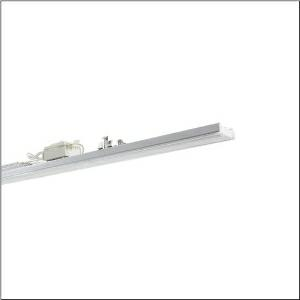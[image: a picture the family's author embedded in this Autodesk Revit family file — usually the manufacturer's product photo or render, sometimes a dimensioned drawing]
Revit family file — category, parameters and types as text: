
# Revit family: licross_r__21_recessed_mo_52te11dv4dxg_417d
name_source: partatom
category: Lighting Fixtures
units: mm (PartAtom-declared; Revit-internal decimal feet)

## family parameters
Cut with Voids When Loaded = No
Host = Face
Light Source = No
Part Type = Normal
Room Calculation Point = No
Round Connector Dimension = Use Diameter
Shared = No

## types (1)
- --- (1 x LED, 13000 lm, 72.2 W, 4000K)
    Apparent Load = 72 VA
    CIE Flux Codes = 89 96 99 100 100
    Color Rendering = 80
    Color Temperature = 4000K
    Default Elevation = 1800 mm
    Description = Licross® 21 Recessed MO, luminaire insert, of sheet steel, galvanised, coil coated, white, length: 2.250mm, width: 66mm, height: 67mm, LED rated luminous flux: 13.000lm, light colour: 840, control gear: DALI 2, with plug, 5-pole, with phase selection, mains connection: 220..240V, AC, 50/60Hz, rated input power: 72W, internal wiring halogen-free, primary light control with lens, of plastic, primary optical cover: cover, of PMMA, light emission: direct distribution, primary light characteristic: symmetric, protection rating (complete): IP54, insulation class (complete): insulation class I (protective earthing), certification: CE, ENEC, VDE, UKCA, protection symbol: D if used in an environment with non-conductive dust loads with corresponding accessories, impact resistance: IK06, permissible ambient temperature for indoor applications: -25..+35°C, corresponds to IFS (International Featured Standards) requirements for safety and quality in the food industry, reducing of maximum allowable ambient temperature of 5°C with ceiling mounting, LABS conformity tested according to VDMA 24364:2018-05, packaging unit: 1 piece
    Height = 58 mm
    Lamp = 1 x LED
    Lamp Light Flux = 13000 lm
    Lamp Power = 72.2 W
    Lamp count = 1
    Length = 2250 mm
    Luminous efficacy = 180 lm/W
    Manufacturer = Siteco
    ModVariant = No
    Model = 52TE11DV4DXG
    Mounting Place = Ceiling
    Mounting Type = Pendant
    Number of Poles = 1
    OnlyDefault = Yes
    Power Factor = 1
    Product Name = Licross® 21 Recessed MO
    Product group = luminaire insert | ceiling pendant
    ProductGroupID = 902
    Protection Class = Protection class I
    Protection Degree = IP 54
    RLX_Detail_Level = 1
    RLX_Emergency_Light_Flux = 0 lm
    RLX_Emergency_Type = 0
    RLX_Emergency_Type_DB = No
    RlxData = <blob elided: 29385 chars, md5=b733678d>
    Socket = socket
    Standby Power = 0 W
    System Light Flux = 13000 lm
    System Power = 72 W
    Type Comments = factory setting: luminous flux: 100 % | dim-lin: 254 | 329 mA
    Type Image = l_1296930.jpg
    URL = http://relux.com
    VarID = @adj_148529
    Voltage = 0 V
    Weight = 0.00 kg
    Width = 66 mm

## geometry (parser evidence)
native form markers: Blend x4, Sweep x10
no freeform markers — native parametric forms only
